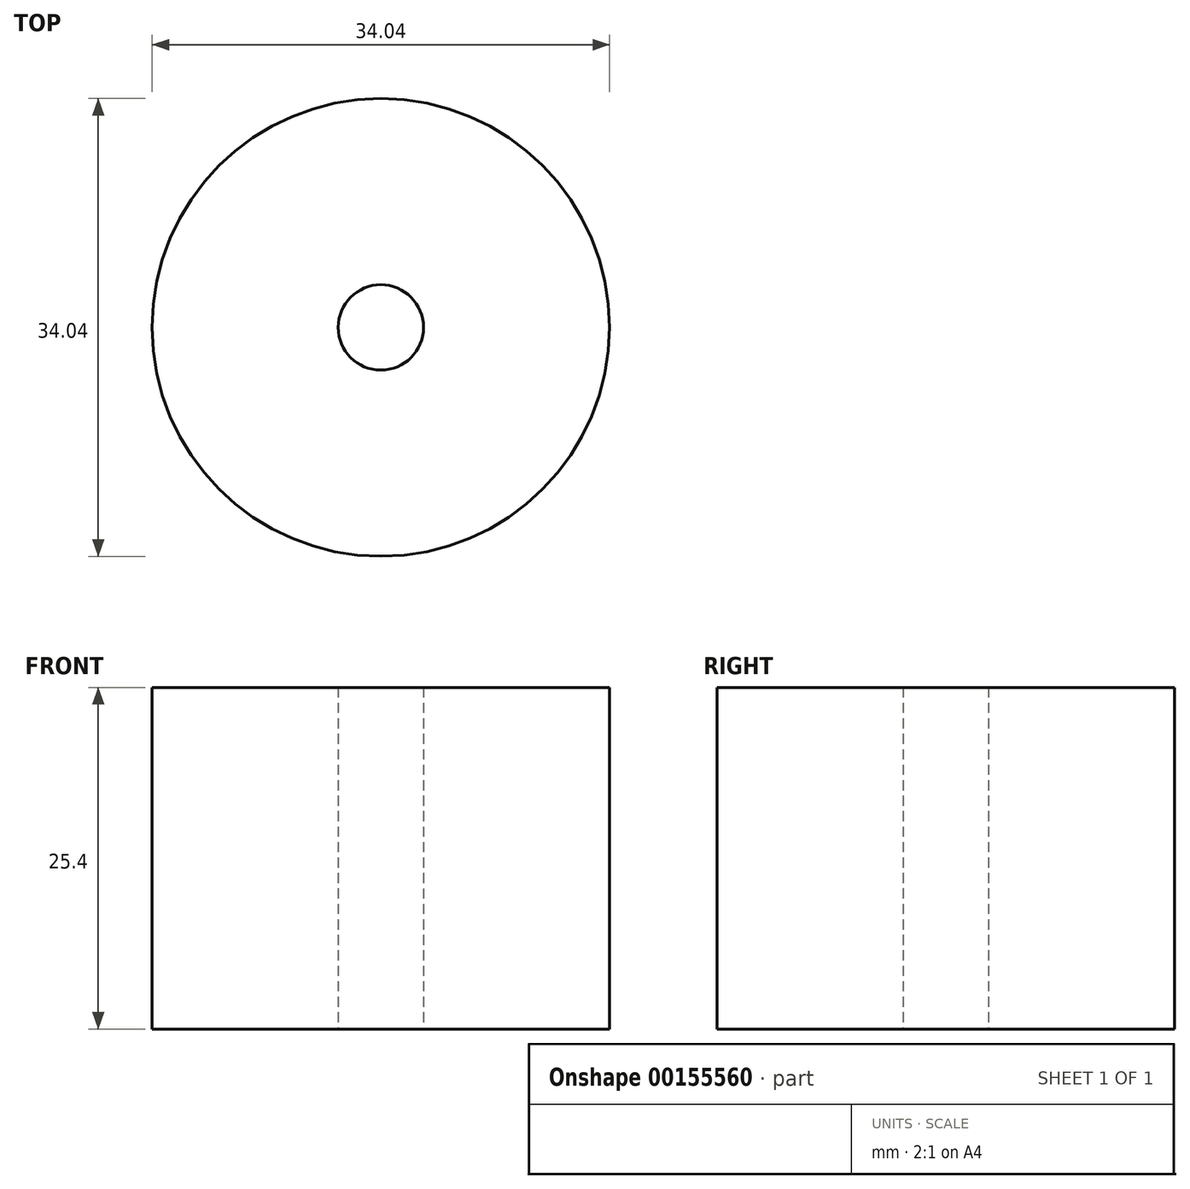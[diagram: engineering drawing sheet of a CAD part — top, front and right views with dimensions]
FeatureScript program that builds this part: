
annotation { "Feature Type Name" : "Feature", "Feature Type Description" : "" }
export const myFeature = defineFeature(function(context is Context, id is Id, definition is map)
    precondition{}
    {
        {
            var Q0;
            Q0=qCreatedBy(makeId("Top.planeOp"),FACE);
            var sketch = newSketch(context, id + "F0", { "sketchPlane" : qUnion([Q0])});
            skCircle(sketch, "E0", {"center": v(0, 0) * mm, "radius": 17.02 * mm});
            skCircle(sketch, "E1", {"center": v(0, 0) * mm, "radius": 3.18 * mm});
            skSolve(sketch);
        }
        {
            var Q0;
            Q0=makeQuery(id+"F0.imprint","IMPRINT",FACE,{"disambiguationData":[TD([[makeQuery(id+"F0.imprint","IMPRINT",EDGE,{"derivedFrom":sQuery(id+"F0.wireOp",EDGE,"E0")}),1.0]])]});
            extrude(context, id + "F1", {"entities" : qUnion([Q0]), "depth" : 25.4 * mm});
        }
    });
